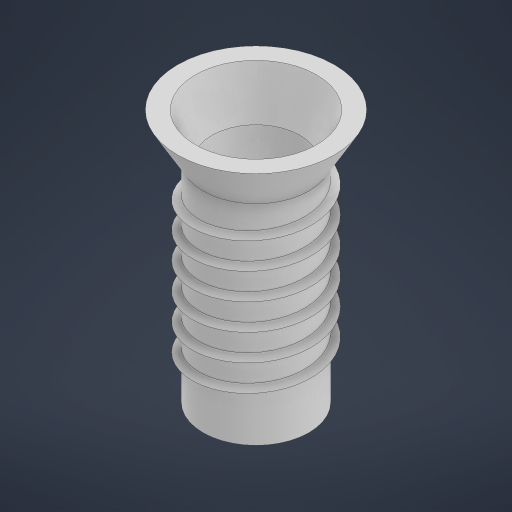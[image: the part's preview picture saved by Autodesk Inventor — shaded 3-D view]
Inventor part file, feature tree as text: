
AUTODESK INVENTOR PART (.ipt)
format: ipt  version: 2024.1 (Build 281209000, 209)  size: 606,720 bytes
history: native  units: mm
features: sketch x3, revolve x2, helix x1
ambient origin geometry x8: Origin, YZ Plane, XZ Plane, XY Plane, X Axis, Y Axis, Z Axis, Center Point
bodies: Solid1 (feature_tree)
feature tree (6):
  revolve  "Revolution1"  [1 undecoded]
  helix  "Coil1"  [1 undecoded]
  revolve  "Revolution2"  [1 undecoded]
  sketch  "Sketch1"  dims[d0=2.5mm d1=12.0mm d2=8.0mm]
  sketch  "Sketch2"  dims[d3=2.0mm d4=47.5mm]
  sketch  "Sketch3"  dims[d5=90.0deg d6=60.0deg d7=1.8mm d8=3.0mm d9=6.0mm d10=10.0mm d11=60.0mm d12=0.0mm d13=90.0deg d14=90.0deg d15=0.0mm d16=0.0mm d17=120.0deg d18=4.0mm d19=10.0mm d20=90.0deg]
note: 3 required parameter values undecoded (feature->parameter linkage not recoverable at this tier; creation-order binding heuristic only, values carry confidence <= 0.55)